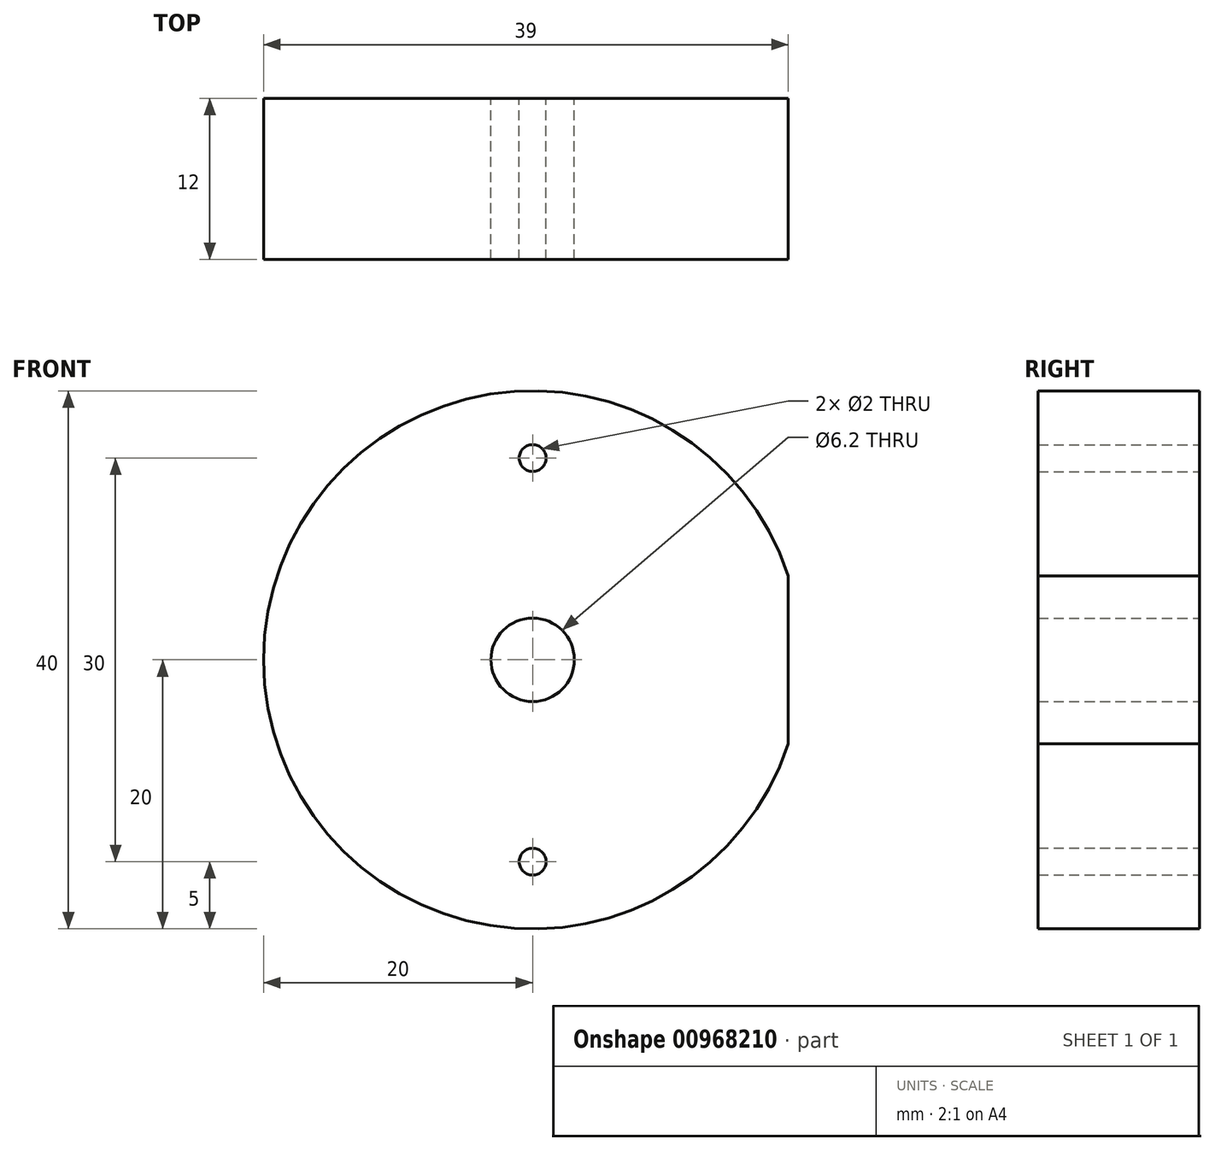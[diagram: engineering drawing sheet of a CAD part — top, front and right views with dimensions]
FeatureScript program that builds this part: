
annotation { "Feature Type Name" : "Feature", "Feature Type Description" : "" }
export const myFeature = defineFeature(function(context is Context, id is Id, definition is map)
    precondition{}
    {
        {
            var Q0;
            Q0=qCreatedBy(makeId("Front.planeOp"),FACE);
            var sketch = newSketch(context, id + "F0", { "sketchPlane" : qUnion([Q0])});
            skArc(sketch, "E0", {"start": v(19, 6.24) * mm, "mid": v(-20, 0) * mm, "end": v(19, -6.24) * mm});
            skCircle(sketch, "E1", {"center": v(0, 0) * mm, "radius": 3.1 * mm});
            skCircle(sketch, "E2", {"center": v(0, 15) * mm, "radius": 1 * mm});
            skCircle(sketch, "E3", {"center": v(0, -15) * mm, "radius": 1 * mm});
            skLineSegment(sketch, "E4", {"start": v(19, 6.24) * mm, "end": v(19, -6.24) * mm});
            skSolve(sketch);
        }
        {
            var Q0;
            Q0=makeQuery(id+"F0.imprint","IMPRINT",FACE,{"disambiguationData":[TD([[makeQuery(id+"F0.imprint","IMPRINT",EDGE,{"derivedFrom":sQuery(id+"F0.wireOp",EDGE,"E0")}),1.0]])]});
            extrude(context, id + "F1", {"entities" : qUnion([Q0]), "endBound" : BoundingType.SYMMETRIC, "depth" : 12 * mm, "offsetDistance" : 25 * mm});
        }
    });
